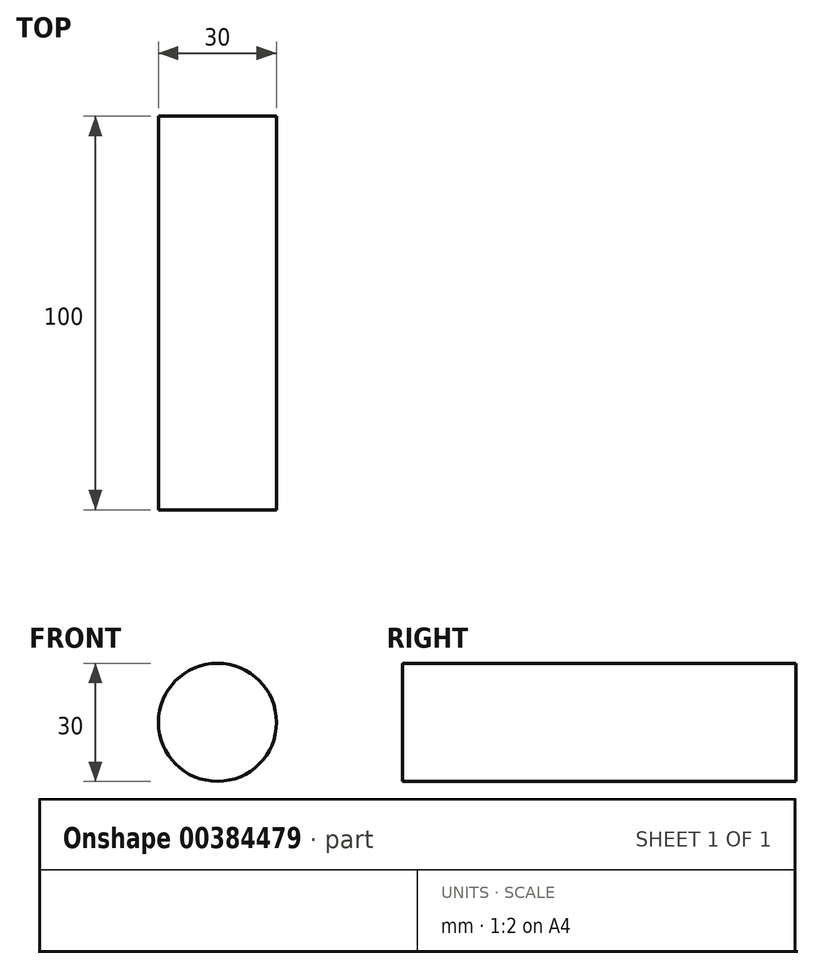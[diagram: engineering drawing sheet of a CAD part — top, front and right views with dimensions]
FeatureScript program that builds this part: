
annotation { "Feature Type Name" : "Feature", "Feature Type Description" : "" }
export const myFeature = defineFeature(function(context is Context, id is Id, definition is map)
    precondition{}
    {
        {
            var Q0;
            Q0=qCreatedBy(makeId("Right.planeOp"),FACE);
            var sketch = newSketch(context, id + "F0", { "sketchPlane" : qUnion([Q0])});
            skLineSegment(sketch, "E0.bottom", {"start": v(-50, 15) * mm, "end": v(50, 15) * mm});
            skLineSegment(sketch, "E0.top", {"start": v(-50, 0) * mm, "end": v(50, 0) * mm});
            skLineSegment(sketch, "E0.left", {"start": v(-50, 15) * mm, "end": v(-50, 0) * mm});
            skLineSegment(sketch, "E0.right", {"start": v(50, 15) * mm, "end": v(50, 0) * mm});
            skLineSegment(sketch, "E1", {"start": v(-55.87, 0) * mm, "end": v(73.88, 0) * mm, "construction": true});
            skSolve(sketch);
        }
        {
            var Q0;
            Q0=makeQuery(id+"F0.imprint","IMPRINT",FACE,{"disambiguationData":[TD([[makeQuery(id+"F0.imprint","IMPRINT",EDGE,{"derivedFrom":sQuery(id+"F0.wireOp",EDGE,"E0.bottom")}),-1.0]])]});
            var Q1;
            Q1=sQuery(id+"F0.wireOp",EDGE,"E0.top");
            revolve(context, id + "F1", {"entities" : qUnion([Q0]), "axis" : qUnion([Q1]), "revolveType" : RevolveType.FULL});
        }
    });
